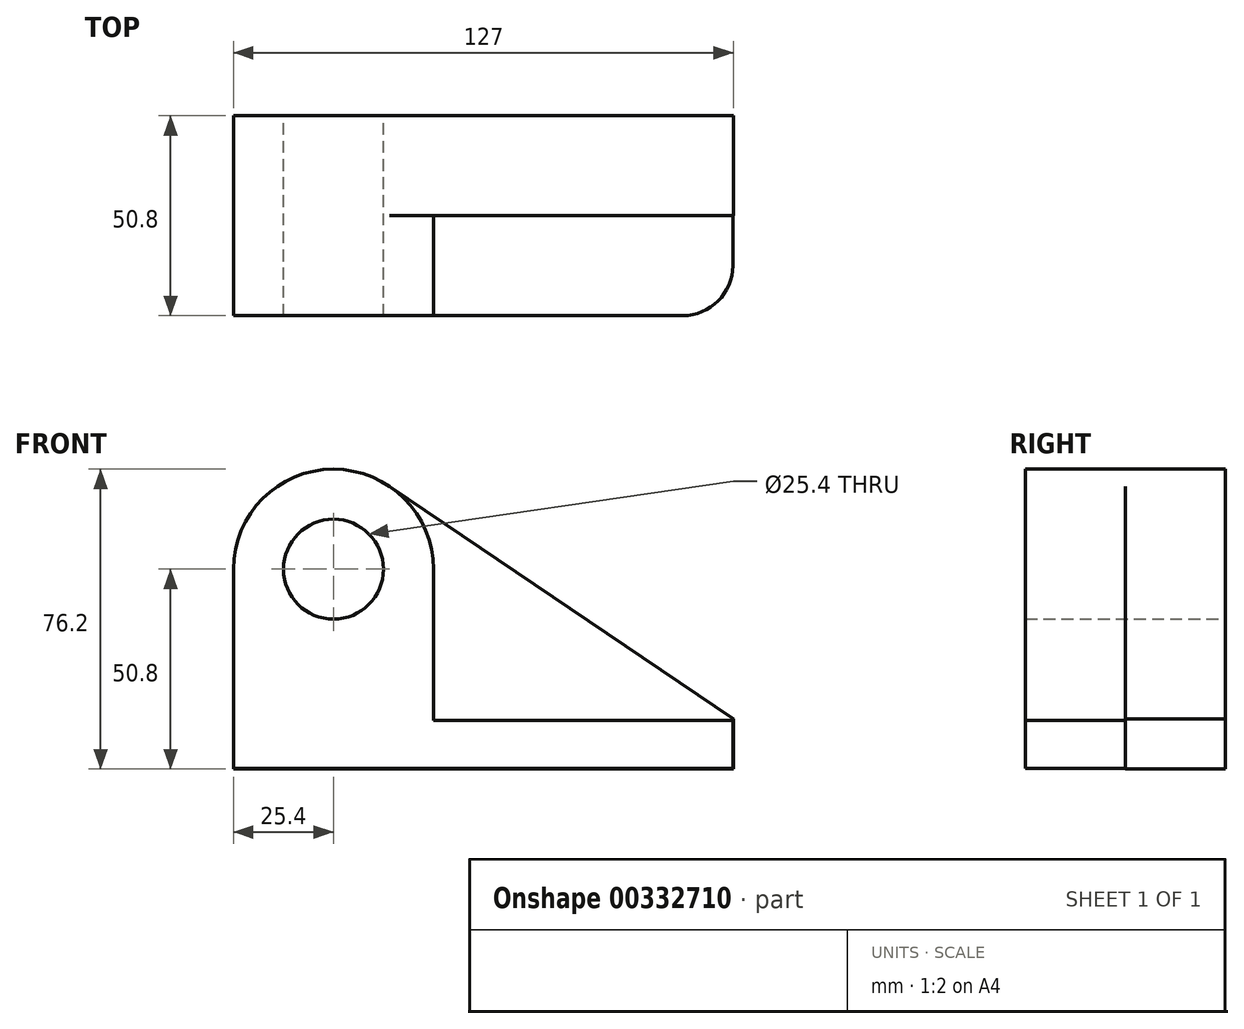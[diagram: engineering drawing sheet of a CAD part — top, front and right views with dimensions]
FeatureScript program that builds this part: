
annotation { "Feature Type Name" : "Feature", "Feature Type Description" : "" }
export const myFeature = defineFeature(function(context is Context, id is Id, definition is map)
    precondition{}
    {
        {
            var Q0;
            Q0=qCreatedBy(makeId("Front.planeOp"),FACE);
            var sketch = newSketch(context, id + "F0", { "sketchPlane" : qUnion([Q0])});
            skCircle(sketch, "E0", {"center": v(0, 0) * mm, "radius": 12.7 * mm});
            skArc(sketch, "E1", {"start": v(14.24, 21.03) * mm, "mid": v(-11.9, 22.44) * mm, "end": v(-25.4, 0) * mm});
            skLineSegment(sketch, "E2", {"start": v(-25.4, 0) * mm, "end": v(-25.4, -50.8) * mm});
            skLineSegment(sketch, "E3", {"start": v(-25.4, -50.8) * mm, "end": v(101.6, -50.8) * mm});
            skLineSegment(sketch, "E4", {"start": v(101.6, -50.8) * mm, "end": v(101.6, -38.1) * mm});
            skLineSegment(sketch, "E5", {"start": v(101.6, -38.1) * mm, "end": v(14.24, 21.03) * mm});
            skSolve(sketch);
        }
        {
            var Q0;
            Q0 = qSketchRegion(id + "F0", true);
            extrude(context, id + "F1", {"entities" : qUnion([Q0]), "depth" : 25.4 * mm});
        }
        {
            var Q0;
            Q0=makeQuery(id+"F1.opExtrude","CAP_FACE",FACE,{"disambiguationData":[OSD([sQuery(id+"F0.wireOp",EDGE,"E0"),sQuery(id+"F0.wireOp",EDGE,"E1"),sQuery(id+"F0.wireOp",EDGE,"E2"),sQuery(id+"F0.wireOp",EDGE,"E3"),sQuery(id+"F0.wireOp",EDGE,"E4"),sQuery(id+"F0.wireOp",EDGE,"E5")])],"isStart":false});
            var sketch = newSketch(context, id + "F2", { "sketchPlane" : qUnion([Q0])});
            skArc(sketch, "E6", {"start": v(25.4, 0) * mm, "mid": v(0, 25.4) * mm, "end": v(-25.4, 0) * mm});
            skLineSegment(sketch, "E7.bottom", {"start": v(101.44, -38.38) * mm, "end": v(25.4, -38.38) * mm});
            skLineSegment(sketch, "E7.top", {"start": v(101.44, -50.65) * mm, "end": v(-25.56, -50.65) * mm});
            skLineSegment(sketch, "E7.left", {"start": v(101.44, -38.38) * mm, "end": v(101.44, -50.65) * mm});
            skLineSegment(sketch, "E7.right", {"start": v(-25.56, -38.38) * mm, "end": v(-25.56, -50.65) * mm});
            skLineSegment(sketch, "E8", {"start": v(25.4, 0) * mm, "end": v(25.4, -38.38) * mm});
            skSolve(sketch);
        }
        {
            var Q0;
            Q0=makeQuery(id+"F2.imprint","IMPRINT",FACE,{"disambiguationData":[TD([[makeQuery(id+"F2.imprint","IMPRINT",EDGE,{"derivedFrom":sQuery(id+"F2.wireOp",EDGE,"E7.bottom")}),1.0]])]});
            extrude(context, id + "F3", {"entities" : qUnion([Q0]), "operationType" : NewBodyOperationType.ADD, "depth" : 25.4 * mm});
        }
        {
            var Q0;
            Q0=makeQuery(id+"F3.opExtrude","CAP_EDGE",EDGE,{"disambiguationData":[OSD([sQuery(id+"F2.wireOp",EDGE,"E7.left")])],"isStart":false});
            fillet(context, id + "F4", {"entities" : qUnion([Q0]), "radius" : 12.7 * mm, "tangentPropagation" : true, "allowEdgeOverflow" : false});
        }
    });
